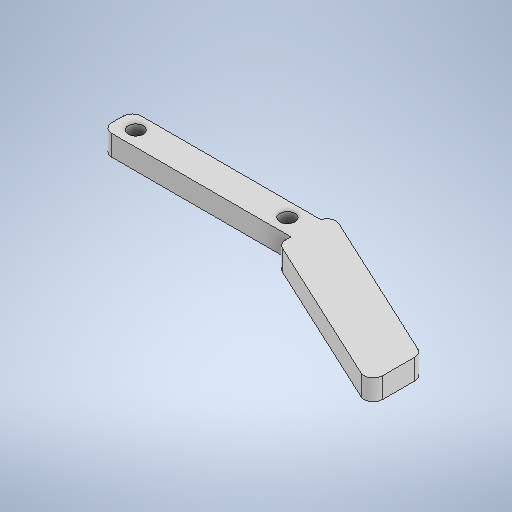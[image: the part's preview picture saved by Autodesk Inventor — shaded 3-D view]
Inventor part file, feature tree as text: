
AUTODESK INVENTOR PART (.ipt)
format: ipt  version: 2025.1 (Build 291241020, 241B)  size: 765,440 bytes
history: native  units: in
note: dims shown in document units (in); Inventor stores cm internally (conversion verified against a paired STEP export)
features: extrude x17, sketch x17, fillet x4, other x3, pattern_circular x1
ambient origin geometry x8: Origin, YZ Plane, XZ Plane, XY Plane, X Axis, Y Axis, Z Axis, Center Point
bodies: Solid1 (feature_tree)
feature tree (42):
  other  "servoMoldAssembly.iam"
  other  "block.ipt:1"
  other  "sg90horn.ipt:1"
  extrude  "Extrusion1"  Depth=0.3937in TaperAngle=0.0deg
  extrude  "Extrusion2"  Depth=0.3937in TaperAngle=0.0deg
  extrude  "Extrusion3"  Depth=0.0591in TaperAngle=0.0deg
  extrude  "Extrusion4"  Depth=0.0591in TaperAngle=0.0deg
  extrude  "Extrusion5"  Depth=1.9685in
  extrude  "Extrusion6"  Depth=0.3937in TaperAngle=0.0deg
  extrude  "Extrusion7"  Depth=0.3937in TaperAngle=0.0deg
  extrude  "Extrusion8"  Depth=0.1299in
  extrude  "Extrusion10"  Depth=0.0787in TaperAngle=0.0deg
  extrude  "Extrusion11"  Depth=0.0787in TaperAngle=0.0deg
  fillet  "Fillet1"  Radius=0.0787in
  extrude  "Extrusion12"  Depth=0.8268in
  fillet  "Fillet2"  Radius=1.1934in
  extrude  "Extrusion13"  TaperAngle=90.0deg  [1 undecoded]
  pattern_circular  "Circular Pattern2"  Count=20 Angle=240.0deg
  extrude  "Extrusion14"  Depth=0.3937in
  extrude  "Extrusion15"  Depth=0.3937in
  extrude  "Extrusion16"  Depth=0.0787in
  fillet  "Fillet3"  Radius=1.3032in
  extrude  "Extrusion17"  Depth=0.0787in
  extrude  "Extrusion18"  Depth=0.0787in
  fillet  "Fillet4"  Radius=0.3937in
  sketch  "Sketch3"  dims[d0=0.3937in d1=0.3937in d2=0.0in]
  sketch  "Sketch4"  dims[d3=0.2795in d4=0.3937in d5=0.0in]
  sketch  "Sketch5"  dims[d6=0.0591in d7=0.0in d8=0.0591in d9=0.0in]
  sketch  "Sketch6"  dims[d10=0.0591in d11=0.0in d12=0.0591in d13=0.0in]
  sketch  "Sketch7"  dims[d14=1.4173in d15=1.9685in]
  sketch  "Sketch8"  dims[d16=0.0in d17=0.3937in d18=0.0in]
  sketch  "Sketch9"  dims[d19=0.3937in d20=0.0in d29=0.2362in d30=0.0in]
  sketch  "Sketch10"  dims[d31=0.2362in d32=0.1299in]
  sketch  "Sketch12"  dims[d33=0.0787in d34=0.2362in d35=0.0in]
  sketch  "Sketch13"  dims[d36=0.0787in d37=0.2362in d38=0.0in d39=0.0787in]
  sketch  "Sketch14"  dims[d40=0.0984in d41=0.8268in d42=1.1934in]
  sketch  "Sketch15"  dims[d43=0.0591in d44=90.0deg]
  sketch  "Sketch16"  dims[d45=0.3937in d46=0.0in d47=7.874in d48=240.0deg]
  sketch  "Sketch17"  dims[d50=0.3937in d51=0.0in d52=0.1299in]
  sketch  "Sketch18"  dims[d53=0.3937in d54=0.0in d55=0.1575in]
  sketch  "Sketch19"  dims[d56=0.3937in d57=0.0in d58=0.0787in d60=1.3032in]
  sketch  "Sketch20"  dims[d61=0.1299in d62=0.1575in d63=0.0in d64=0.3937in d65=0.0in d66=1.5748in d67=0.1718in d68=1.5748in d69=0.1718in d70=0.0984in d71=1.5748in d72=0.4528in d73=0.3937in d74=0.0in d75=0.0787in]
note: 1 required parameter value undecoded (feature->parameter linkage not recoverable at this tier; creation-order binding heuristic only, values carry confidence <= 0.55)
